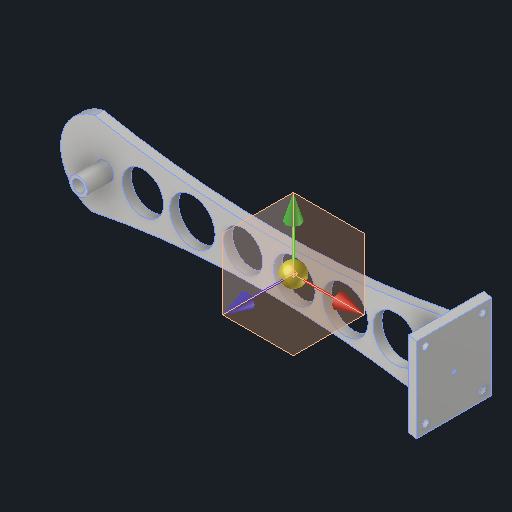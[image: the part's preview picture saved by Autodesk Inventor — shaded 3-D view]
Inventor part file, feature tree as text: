
AUTODESK INVENTOR PART (.ipt)
format: ipt  version: 2023.4 (Build 274418000, 418)  size: 217,600 bytes
history: native  units: mm
features: sketch x14, extrude x8
ambient origin geometry x8: Origin, YZ Plane, XZ Plane, XY Plane, X Axis, Y Axis, Z Axis, Center Point
bodies: Solid1 (feature_tree)
feature tree (22):
  extrude  "Extrusion1"  Depth=40.0mm
  extrude  "Extrusion2"  Depth=400.0mm
  extrude  "Extrusion3"  Depth=4.0mm TaperAngle=0.0deg
  extrude  "Extrusion4"  Depth=11.9mm TaperAngle=0.0deg
  extrude  "Extrusion5"  Depth=5.0mm TaperAngle=0.0deg
  sketch  "Sketch6"  dims[d19=15.0mm d20=0.0mm d21=35.0mm d22=0.0mm]
  sketch  "Sketch7"  dims[d23=19.0mm d24=0.0mm d27=2.95mm]
  sketch  "Sketch8"  dims[d28=2.95mm d29=2.95mm]
  extrude  "Extrusion6"  Depth=15.0mm TaperAngle=0.0deg
  sketch  "Sketch10"  dims[d31=4.0mm]
  sketch  "Sketch11"  dims[d32=4.0mm]
  sketch  "Sketch12"  dims[d33=4.0mm]
  extrude  "Extrusion7"  Depth=19.0mm
  extrude  "Extrusion8"  Depth=2.95mm
  sketch  "Sketch1"  dims[d5=40.0mm d6=40.0mm]
  sketch  "Sketch2"  dims[d7=150.0mm d8=400.0mm]
  sketch  "Sketch3"  dims[d9=400.0mm d10=4.0mm d11=0.0mm]
  sketch  "Sketch4"  dims[d12=8.0mm d13=10.75mm d14=11.9mm d15=0.0mm]
  sketch  "Sketch5"  dims[d16=5.5mm d17=5.0mm d18=0.0mm]
  sketch  "Sketch9"  dims[d30=2.95mm]
  sketch  "Sketch13"  dims[d34=4.0mm]
  sketch  "Sketch14"  dims[d35=4.0mm d36=4.0mm d37=4.0mm d38=4.0mm d39=5.0mm d40=0.0mm d41=10.0mm d42=0.0mm d43=1.0mm d44=1.0mm d45=0.1mm d46=0.0mm]
